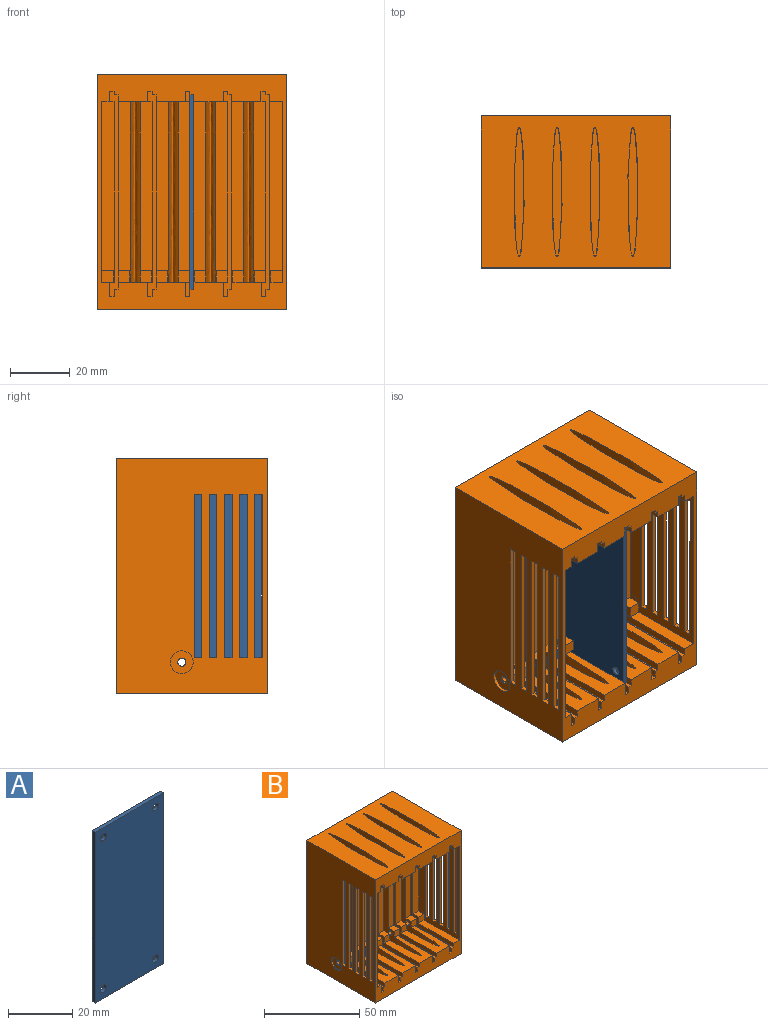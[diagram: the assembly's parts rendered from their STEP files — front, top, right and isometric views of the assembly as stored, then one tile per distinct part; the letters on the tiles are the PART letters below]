
ASSEMBLY  parts=2 mates=1
PART A: 10 faces, bbox 30.1x1.3x65 mm
  f0: plane 64.99x1.33mm, normal (-1,0,0), area 86.7mm2, adj f1,f6,f8,f9
  f1: plane 30.14x1.33mm, normal (0,0,-1), area 40.2mm2, adj f0,f2,f8,f9
  f2: plane 64.99x1.33mm, normal (1,0,0), area 86.7mm2, adj f1,f6,f8,f9
  f3: cylinder r=1.33mm len=2.67mm, axis (0,1,0), area 11.2mm2, adj f8,f9
  f4: cylinder r=1.33mm len=2.67mm, axis (0,1,0), area 11.2mm2, adj f8,f9
  f5: cylinder r=1.33mm len=2.67mm, axis (0,1,0), area 11.2mm2, adj f8,f9
  f6: plane 30.14x1.33mm, normal (0,0,1), area 40.2mm2, adj f0,f2,f8,f9
  f7: cylinder r=1.33mm len=2.67mm, axis (0,1,0), area 11.2mm2, adj f8,f9
  f8: plane 64.99x30.14mm, normal (0,-1,0), area 1936.1mm2, adj f0,f1,f2,f3,f4,f5,f6,f7
  f9: plane 64.99x30.14mm, normal (0,1,0), area 1936.1mm2, adj f0,f1,f2,f3,f4,f5,f6,f7
PART B: 226 faces, bbox 63.5x50.8x79 mm
  f0: plane 30.14x3.22mm, normal (0,0,1), area 76.3mm2, adj f1,f2,f23,f25,f28,f77,f100,f106
  f1: cylinder r=1.38mm len=1mm, axis (1,0,0), area 0.6mm2, adj f0,f23,f106,f223
  f2: cylinder r=1.38mm len=2.71mm, axis (1,0,0), area 2.2mm2, adj f0,f28,f106,f223
  f3: plane 1x0.99mm, normal (-1,0,0), area 0.3mm2, adj f53,f102,f220
  f4: plane 78.99x50.8mm, normal (1,0,0), area 3273.6mm2, adj f98,f99,f100,f101,f176,f177,f178,f179
  f5: plane 2.55x1.31mm, normal (0,0,-1), area 3.4mm2, adj f35,f72,f129,f200
  f6: plane 2.55x1.31mm, normal (0,0,-1), area 3.4mm2, adj f37,f67,f133,f205
  f7: plane 2.55x1.31mm, normal (0,0,-1), area 3.4mm2, adj f39,f62,f137,f210
  f8: plane 2.55x1.31mm, normal (0,0,-1), area 3.4mm2, adj f41,f57,f141,f215
  f9: plane 1x0.99mm, normal (-1,0,0), area 0.3mm2, adj f50,f110,f199
  f10: plane 1x0.99mm, normal (1,0,0), area 0.3mm2, adj f30,f109,f202
  f11: plane 1x0.99mm, normal (-1,0,0), area 0.3mm2, adj f48,f114,f204
  f12: plane 1x0.99mm, normal (1,0,0), area 0.3mm2, adj f31,f113,f207
  f13: plane 1x0.99mm, normal (-1,0,0), area 0.3mm2, adj f46,f118,f209
  f14: plane 1x0.99mm, normal (1,0,0), area 0.3mm2, adj f32,f117,f212
  f15: plane 1x0.99mm, normal (-1,0,0), area 0.3mm2, adj f44,f122,f214
  f16: plane 1x0.99mm, normal (1,0,0), area 0.3mm2, adj f33,f121,f217
  f17: plane 1x0.99mm, normal (1,0,0), area 0.3mm2, adj f53,f102,f219
  f18: plane 1x0.99mm, normal (-1,0,0), area 0.3mm2, adj f53,f102,f219
  f19: extruded ~76.2x43.34mm, area 3513.7mm2, adj f33,f40,f41,f43,f44,f98,f122,f140
  f20: extruded ~76.2x43.34mm, area 3513.7mm2, adj f32,f38,f39,f45,f46,f98,f118,f136
  f21: extruded ~76.2x43.34mm, area 3513.7mm2, adj f31,f36,f37,f47,f48,f98,f114,f132
  f22: extruded ~76.2x43.34mm, area 3513.7mm2, adj f30,f34,f35,f49,f50,f98,f110,f128
  f23: plane 1x0.99mm, normal (1,0,0), area 0.3mm2, adj f0,f1,f106
  f24: plane 3.29x1.44mm, normal (0,0,-1), area 4.6mm2, adj f26,f77,f103,f106,f147,f197
  f25: plane 1x0.99mm, normal (-1,0,0), area 0.3mm2, adj f0,f106,f197
  f26: plane 1x0.99mm, normal (1,0,0), area 0.3mm2, adj f24,f106,f197
  f27: plane 60.39x30.14mm, normal (-1,0,0), area 1120mm2, adj f52,f53,f100,f102,f176,f177,f178,f179
  f28: plane 60.39x30.14mm, normal (1,0,0), area 1120mm2, adj f0,f2,f51,f100,f106,f156,f157,f158
  f29: plane 78.99x50.8mm, normal (-1,0,0), area 3273.6mm2, adj f98,f99,f100,f101,f156,f157,f158,f159
  f30: plane 60.39x4.01mm, normal (0,-1,0), area 229.8mm2, adj f10,f22,f34,f49,f107,f108,f109,f129
  f31: plane 60.39x4.01mm, normal (0,-1,0), area 229.8mm2, adj f12,f21,f36,f47,f111,f112,f113,f133
  f32: plane 60.39x4.01mm, normal (0,-1,0), area 229.8mm2, adj f14,f20,f38,f45,f115,f116,f117,f137
  f33: plane 60.39x4.01mm, normal (0,-1,0), area 229.8mm2, adj f16,f19,f40,f43,f119,f120,f121,f141
  f34: plane 4.23x3.88mm, normal (0,0,1), area 16.3mm2, adj f22,f30,f35,f129
  f35: plane 3.84x3.81mm, normal (0,-1,0), area 14.6mm2, adj f5,f22,f34,f50,f129
  f36: plane 4.23x3.88mm, normal (0,0,1), area 16.3mm2, adj f21,f31,f37,f133
  f37: plane 3.84x3.81mm, normal (0,-1,0), area 14.6mm2, adj f6,f21,f36,f48,f133
  f38: plane 4.23x3.88mm, normal (0,0,1), area 16.3mm2, adj f20,f32,f39,f137
  f39: plane 3.84x3.81mm, normal (0,-1,0), area 14.6mm2, adj f7,f20,f38,f46,f137
  f40: plane 4.23x3.88mm, normal (0,0,1), area 16.3mm2, adj f19,f33,f41,f141
  f41: plane 3.84x3.81mm, normal (0,-1,0), area 14.6mm2, adj f8,f19,f40,f44,f141
  f42: plane 32.44x1.34mm, normal (0,0,1), area 43.4mm2, adj f54,f55,f100,f151
  f43: plane 30.14x9.72mm, normal (0,0,-1), area 218.4mm2, adj f19,f33,f58,f94,f100,f122
  f44: plane 30.14x9.92mm, normal (0,0,1), area 200.1mm2, adj f15,f19,f41,f57,f58,f100,f122,f139
  f45: plane 30.14x9.72mm, normal (0,0,-1), area 218.4mm2, adj f20,f32,f63,f90,f100,f118
  f46: plane 30.14x9.92mm, normal (0,0,1), area 200.1mm2, adj f13,f20,f39,f62,f63,f100,f118,f135
  f47: plane 30.14x9.72mm, normal (0,0,-1), area 218.4mm2, adj f21,f31,f68,f86,f100,f114
  f48: plane 30.14x9.92mm, normal (0,0,1), area 200.1mm2, adj f11,f21,f37,f67,f68,f100,f114,f131
  f49: plane 30.14x9.72mm, normal (0,0,-1), area 218.4mm2, adj f22,f30,f73,f82,f100,f110
  f50: plane 30.14x9.92mm, normal (0,0,1), area 200.1mm2, adj f9,f22,f35,f72,f73,f100,f110,f127
  f51: plane 30.14x2.64mm, normal (0,0,-1), area 79.6mm2, adj f28,f78,f100,f106
  f52: plane 30.14x4.36mm, normal (0,0,-1), area 131.4mm2, adj f27,f54,f100,f102
  f53: plane 30.14x4.67mm, normal (0,0,1), area 115.3mm2, adj f3,f17,f18,f27,f54,f100,f102,f143
  f54: plane 64.99x32.44mm, normal (-1,0,0), area 288.2mm2, adj f42,f52,f53,f97,f100,f102,f151
  f55: plane 32.44x2.41mm, normal (-1,0,0), area 78.2mm2, adj f42,f56,f100,f151
  f56: plane 32.44x1.44mm, normal (0,0,1), area 46.8mm2, adj f55,f57,f100,f151
  f57: plane 32.44x4.71mm, normal (1,0,0), area 152.9mm2, adj f8,f44,f56,f100,f121,f151,f216
  f58: plane 64.99x32.44mm, normal (-1,0,0), area 288.1mm2, adj f43,f44,f59,f93,f100,f122,f150
  f59: plane 32.44x1.34mm, normal (0,0,1), area 43.4mm2, adj f58,f60,f100,f150
  f60: plane 32.44x2.41mm, normal (-1,0,0), area 78.3mm2, adj f59,f61,f100,f150
  f61: plane 32.44x1.44mm, normal (0,0,1), area 46.8mm2, adj f60,f62,f100,f150
  f62: plane 32.44x4.71mm, normal (1,0,0), area 152.9mm2, adj f7,f46,f61,f100,f117,f150,f211
  f63: plane 64.99x32.44mm, normal (-1,0,0), area 288.1mm2, adj f45,f46,f64,f89,f100,f118,f149
  f64: plane 32.44x1.34mm, normal (0,0,1), area 43.4mm2, adj f63,f65,f100,f149
  f65: plane 32.44x2.41mm, normal (-1,0,0), area 78.3mm2, adj f64,f66,f100,f149
  f66: plane 32.44x1.44mm, normal (0,0,1), area 46.8mm2, adj f65,f67,f100,f149
  f67: plane 32.44x4.71mm, normal (1,0,0), area 152.9mm2, adj f6,f48,f66,f100,f113,f149,f206
  f68: plane 64.99x32.44mm, normal (-1,0,0), area 288.1mm2, adj f47,f48,f69,f85,f100,f114,f148
  f69: plane 32.44x1.34mm, normal (0,0,1), area 43.4mm2, adj f68,f70,f100,f148
  f70: plane 32.44x2.41mm, normal (-1,0,0), area 78.3mm2, adj f69,f71,f100,f148
  f71: plane 32.44x1.44mm, normal (0,0,1), area 46.8mm2, adj f70,f72,f100,f148
  f72: plane 32.44x4.71mm, normal (1,0,0), area 152.9mm2, adj f5,f50,f71,f100,f109,f148,f201
  f73: plane 64.99x32.44mm, normal (-1,0,0), area 288.1mm2, adj f49,f50,f74,f81,f100,f110,f147
  f74: plane 32.44x1.34mm, normal (0,0,1), area 43.4mm2, adj f73,f75,f100,f147
  f75: plane 32.44x2.41mm, normal (-1,0,0), area 78.3mm2, adj f74,f76,f100,f147
  f76: plane 32.44x1.44mm, normal (0,0,1), area 46.8mm2, adj f75,f77,f100,f147
  f77: plane 32.44x4.71mm, normal (1,0,0), area 152.9mm2, adj f0,f24,f76,f100,f105,f147
  f78: plane 32.44x3.38mm, normal (1,0,0), area 109.6mm2, adj f51,f79,f100,f104,f147
  f79: plane 32.44x1.65mm, normal (0,0,-1), area 53.4mm2, adj f78,f80,f100,f147
  f80: plane 32.44x1.08mm, normal (-1,0,0), area 34.9mm2, adj f79,f81,f100,f147
  f81: plane 32.44x1.34mm, normal (0,0,-1), area 43.4mm2, adj f73,f80,f100,f147
  f82: plane 32.44x3.38mm, normal (1,0,0), area 109.6mm2, adj f49,f83,f100,f108,f148
  f83: plane 32.44x1.65mm, normal (0,0,-1), area 53.4mm2, adj f82,f84,f100,f148
  f84: plane 32.44x1.08mm, normal (-1,0,0), area 34.9mm2, adj f83,f85,f100,f148
  f85: plane 32.44x1.34mm, normal (0,0,-1), area 43.4mm2, adj f68,f84,f100,f148
  f86: plane 32.44x3.38mm, normal (1,0,0), area 109.6mm2, adj f47,f87,f100,f112,f149
  f87: plane 32.44x1.65mm, normal (0,0,-1), area 53.4mm2, adj f86,f88,f100,f149
  f88: plane 32.44x1.08mm, normal (-1,0,0), area 34.9mm2, adj f87,f89,f100,f149
  f89: plane 32.44x1.34mm, normal (0,0,-1), area 43.4mm2, adj f63,f88,f100,f149
  f90: plane 32.44x3.38mm, normal (1,0,0), area 109.6mm2, adj f45,f91,f100,f116,f150
  f91: plane 32.44x1.65mm, normal (0,0,-1), area 53.4mm2, adj f90,f92,f100,f150
  f92: plane 32.44x1.08mm, normal (-1,0,0), area 34.9mm2, adj f91,f93,f100,f150
  f93: plane 32.44x1.34mm, normal (0,0,-1), area 43.4mm2, adj f58,f92,f100,f150
  f94: plane 32.44x3.38mm, normal (1,0,0), area 109.6mm2, adj f43,f95,f100,f120,f151
  f95: plane 32.44x1.65mm, normal (0,0,-1), area 53.4mm2, adj f94,f96,f100,f151
  f96: plane 32.44x1.08mm, normal (-1,0,0), area 34.9mm2, adj f95,f97,f100,f151
  f97: plane 32.44x1.34mm, normal (0,0,-1), area 43.4mm2, adj f54,f96,f100,f151
  f98: plane 63.5x50.8mm, normal (0,0,1), area 2759.6mm2, adj f4,f19,f20,f21,f22,f29,f100,f101
  f99: plane 63.5x50.8mm, normal (0,0,-1), area 3225.8mm2, adj f4,f29,f100,f101
  f100: plane 78.99x63.5mm, normal (0,-1,0), area 1254.7mm2, adj f0,f4,f27,f28,f29,f42,f43,f44
  f101: plane 78.99x63.5mm, normal (0,1,0), area 5016.1mm2, adj f4,f29,f98,f99
  f102: plane 60.39x4.67mm, normal (0,-1,0), area 248.8mm2, adj f3,f17,f18,f27,f52,f53,f54,f144
  f103: plane 60.39x2.3mm, normal (1,0,0), area 138.8mm2, adj f24,f104,f106,f147
  f104: plane 2.3x1.65mm, normal (0,0,1), area 3.8mm2, adj f78,f103,f106,f147
  f105: plane 2.55x1.33mm, normal (0,0,-1), area 3.4mm2, adj f77,f125,f126,f196
  f106: plane 60.39x4.66mm, normal (0,-1,0), area 246.4mm2, adj f0,f1,f2,f23,f24,f25,f26,f28
  f107: plane 60.39x2.3mm, normal (1,0,0), area 138.8mm2, adj f30,f108,f109,f148
  f108: plane 2.3x1.65mm, normal (0,0,1), area 3.8mm2, adj f30,f82,f107,f148
  f109: plane 3.29x1.44mm, normal (0,0,-1), area 4.6mm2, adj f10,f30,f72,f107,f148,f202
  f110: plane 60.39x4.01mm, normal (0,-1,0), area 230.1mm2, adj f9,f22,f49,f50,f73,f127,f128,f198
  f111: plane 60.39x2.3mm, normal (1,0,0), area 138.8mm2, adj f31,f112,f113,f149
  f112: plane 2.3x1.65mm, normal (0,0,1), area 3.8mm2, adj f31,f86,f111,f149
  f113: plane 3.29x1.44mm, normal (0,0,-1), area 4.6mm2, adj f12,f31,f67,f111,f149,f207
  f114: plane 60.39x4.01mm, normal (0,-1,0), area 230.1mm2, adj f11,f21,f47,f48,f68,f131,f132,f203
  f115: plane 60.39x2.3mm, normal (1,0,0), area 138.8mm2, adj f32,f116,f117,f150
  f116: plane 2.3x1.65mm, normal (0,0,1), area 3.8mm2, adj f32,f90,f115,f150
  f117: plane 3.29x1.44mm, normal (0,0,-1), area 4.6mm2, adj f14,f32,f62,f115,f150,f212
  f118: plane 60.39x4.01mm, normal (0,-1,0), area 230.1mm2, adj f13,f20,f45,f46,f63,f135,f136,f208
  f119: plane 60.39x2.3mm, normal (1,0,0), area 138.8mm2, adj f33,f120,f121,f151
  f120: plane 2.3x1.65mm, normal (0,0,1), area 3.8mm2, adj f33,f94,f119,f151
  f121: plane 3.29x1.44mm, normal (0,0,-1), area 4.6mm2, adj f16,f33,f57,f119,f151,f217
  f122: plane 60.39x4.01mm, normal (0,-1,0), area 230.1mm2, adj f15,f19,f43,f44,f58,f139,f140,f213
  f123: plane 4.23x3.81mm, normal (-1,0,0), area 9.9mm2, adj f0,f106,f124,f126,f196
  f124: plane 4.23x4.06mm, normal (0,0,1), area 17.2mm2, adj f106,f123,f125,f126
  f125: plane 4.23x3.81mm, normal (1,0,0), area 9.9mm2, adj f105,f106,f124,f126,f196
  f126: plane 4.06x3.81mm, normal (0,-1,0), area 15.5mm2, adj f0,f105,f123,f124,f125
  f127: plane 4.23x3.81mm, normal (-1,0,0), area 9.9mm2, adj f50,f110,f128,f130,f198
  f128: plane 4.23x3.9mm, normal (0,0,1), area 16.4mm2, adj f22,f110,f127,f130
  f129: plane 4.23x3.81mm, normal (1,0,0), area 9.9mm2, adj f5,f30,f34,f35,f200
  f130: plane 3.86x3.81mm, normal (0,-1,0), area 14.7mm2, adj f22,f50,f127,f128
  f131: plane 4.23x3.81mm, normal (-1,0,0), area 9.9mm2, adj f48,f114,f132,f134,f203
  f132: plane 4.23x3.9mm, normal (0,0,1), area 16.4mm2, adj f21,f114,f131,f134
  f133: plane 4.23x3.81mm, normal (1,0,0), area 9.9mm2, adj f6,f31,f36,f37,f205
  f134: plane 3.86x3.81mm, normal (0,-1,0), area 14.7mm2, adj f21,f48,f131,f132
  f135: plane 4.23x3.81mm, normal (-1,0,0), area 9.9mm2, adj f46,f118,f136,f138,f208
  f136: plane 4.23x3.9mm, normal (0,0,1), area 16.4mm2, adj f20,f118,f135,f138
  f137: plane 4.23x3.81mm, normal (1,0,0), area 9.9mm2, adj f7,f32,f38,f39,f210
  f138: plane 3.86x3.81mm, normal (0,-1,0), area 14.7mm2, adj f20,f46,f135,f136
  f139: plane 4.23x3.81mm, normal (-1,0,0), area 9.9mm2, adj f44,f122,f140,f142,f213
  f140: plane 4.23x3.9mm, normal (0,0,1), area 16.4mm2, adj f19,f122,f139,f142
  f141: plane 4.23x3.81mm, normal (1,0,0), area 9.9mm2, adj f8,f33,f40,f41,f215
  f142: plane 3.86x3.81mm, normal (0,-1,0), area 14.7mm2, adj f19,f44,f139,f140
  f143: plane 4.06x3.81mm, normal (0,-1,0), area 15.5mm2, adj f53,f144,f145,f146
  f144: plane 4.23x3.81mm, normal (1,0,0), area 9.9mm2, adj f53,f102,f143,f145,f218
  f145: plane 4.23x4.06mm, normal (0,0,1), area 17.2mm2, adj f102,f143,f144,f146
  f146: plane 4.23x3.81mm, normal (-1,0,0), area 9.9mm2, adj f53,f102,f143,f145,f218
  f147: plane 68.48x2.98mm, normal (0,-1,0), area 99.4mm2, adj f24,f73,f74,f75,f76,f77,f78,f79
  f148: plane 68.48x2.98mm, normal (0,-1,0), area 99.4mm2, adj f68,f69,f70,f71,f72,f82,f83,f84
  f149: plane 68.48x2.98mm, normal (0,-1,0), area 99.4mm2, adj f63,f64,f65,f66,f67,f86,f87,f88
  f150: plane 68.48x2.98mm, normal (0,-1,0), area 99.4mm2, adj f58,f59,f60,f61,f62,f90,f91,f92
  f151: plane 68.48x2.98mm, normal (0,-1,0), area 99.4mm2, adj f42,f54,f55,f56,f57,f94,f95,f96
  f152: plane 43.34x3.42mm, normal (0,0,1), area 116.6mm2, adj f19
  f153: plane 43.34x3.42mm, normal (0,0,1), area 116.6mm2, adj f20
  f154: plane 43.34x3.42mm, normal (0,0,1), area 116.6mm2, adj f21
  f155: plane 43.34x3.42mm, normal (0,0,1), area 116.6mm2, adj f22
  f156: plane 54.63x1.39mm, normal (0,1,0), area 76mm2, adj f28,f29,f157,f159
  f157: plane 2.54x1.39mm, normal (0,0,1), area 3.5mm2, adj f28,f29,f156,f158
  f158: plane 54.63x1.39mm, normal (0,-1,0), area 76mm2, adj f28,f29,f157,f159
  f159: plane 2.54x1.39mm, normal (0,0,-1), area 3.5mm2, adj f28,f29,f156,f158
  f160: plane 54.63x1.39mm, normal (0,1,0), area 76mm2, adj f28,f29,f161,f163
  f161: plane 2.54x1.39mm, normal (0,0,1), area 3.5mm2, adj f28,f29,f160,f162
  f162: plane 54.63x1.39mm, normal (0,-1,0), area 76mm2, adj f28,f29,f161,f163
  f163: plane 2.54x1.39mm, normal (0,0,-1), area 3.5mm2, adj f28,f29,f160,f162
  f164: plane 54.63x1.39mm, normal (0,1,0), area 76mm2, adj f28,f29,f165,f167
  f165: plane 2.54x1.39mm, normal (0,0,1), area 3.5mm2, adj f28,f29,f164,f166
  f166: plane 54.63x1.39mm, normal (0,-1,0), area 76mm2, adj f28,f29,f165,f167
  f167: plane 2.54x1.39mm, normal (0,0,-1), area 3.5mm2, adj f28,f29,f164,f166
  f168: plane 54.63x1.39mm, normal (0,1,0), area 76mm2, adj f28,f29,f169,f171
  f169: plane 2.54x1.39mm, normal (0,0,1), area 3.5mm2, adj f28,f29,f168,f170
  f170: plane 54.63x1.39mm, normal (0,-1,0), area 76mm2, adj f28,f29,f169,f171
  f171: plane 2.54x1.39mm, normal (0,0,-1), area 3.5mm2, adj f28,f29,f168,f170
  f172: plane 54.63x1.39mm, normal (0,1,0), area 76mm2, adj f28,f29,f173,f175
  f173: plane 2.54x1.39mm, normal (0,0,1), area 3.5mm2, adj f28,f29,f172,f174
  f174: plane 54.63x1.39mm, normal (0,-1,0), area 76mm2, adj f28,f29,f173,f175
  f175: plane 2.54x1.39mm, normal (0,0,-1), area 3.5mm2, adj f28,f29,f172,f174
  f176: plane 2.54x1.33mm, normal (0,0,-1), area 3.4mm2, adj f4,f27,f177,f179
  f177: plane 54.63x1.39mm, normal (0,-1,0), area 74.1mm2, adj f4,f27,f176,f178
  f178: plane 2.54x1.39mm, normal (0,0,1), area 3.5mm2, adj f4,f27,f177,f179
  f179: plane 54.63x1.39mm, normal (0,1,0), area 74.1mm2, adj f4,f27,f176,f178
  f180: plane 2.54x1.33mm, normal (0,0,-1), area 3.4mm2, adj f4,f27,f181,f183
  f181: plane 54.63x1.39mm, normal (0,-1,0), area 74.1mm2, adj f4,f27,f180,f182
  f182: plane 2.54x1.39mm, normal (0,0,1), area 3.5mm2, adj f4,f27,f181,f183
  f183: plane 54.63x1.39mm, normal (0,1,0), area 74.1mm2, adj f4,f27,f180,f182
  f184: plane 2.54x1.33mm, normal (0,0,-1), area 3.4mm2, adj f4,f27,f185,f187
  f185: plane 54.63x1.39mm, normal (0,-1,0), area 74.1mm2, adj f4,f27,f184,f186
  f186: plane 2.54x1.39mm, normal (0,0,1), area 3.5mm2, adj f4,f27,f185,f187
  f187: plane 54.63x1.39mm, normal (0,1,0), area 74.1mm2, adj f4,f27,f184,f186
  f188: plane 2.54x1.33mm, normal (0,0,-1), area 3.4mm2, adj f4,f27,f189,f191
  f189: plane 54.63x1.39mm, normal (0,-1,0), area 74.1mm2, adj f4,f27,f188,f190
  f190: plane 2.54x1.39mm, normal (0,0,1), area 3.5mm2, adj f4,f27,f189,f191
  f191: plane 54.63x1.39mm, normal (0,1,0), area 74.1mm2, adj f4,f27,f188,f190
  f192: plane 2.54x1.33mm, normal (0,0,-1), area 3.4mm2, adj f4,f27,f193,f195
  f193: plane 54.63x1.39mm, normal (0,-1,0), area 74.1mm2, adj f4,f27,f192,f194
  f194: plane 2.54x1.39mm, normal (0,0,1), area 3.5mm2, adj f4,f27,f193,f195
  f195: plane 54.63x1.39mm, normal (0,1,0), area 74.1mm2, adj f4,f27,f192,f194
  f196: cylinder r=1.38mm len=4.06mm, axis (1,0,0), area 23.5mm2, adj f0,f105,f106,f123,f125
  f197: cylinder r=1.38mm len=4.06mm, axis (1,0,0), area 6mm2, adj f0,f24,f25,f26,f106
  f198: cylinder r=1.38mm len=3.9mm, axis (-1,0,0), area 22.5mm2, adj f22,f50,f110,f127
  f199: cylinder r=1.38mm len=3.9mm, axis (-1,0,0), area 5.7mm2, adj f9,f22,f50,f110
  f200: cylinder r=1.38mm len=3.88mm, axis (-1,0,0), area 22.4mm2, adj f5,f22,f30,f129,f201
  f201: plane 2.55x0.69mm, normal (0,0,1), area 1.8mm2, adj f22,f72,f200,f202
  f202: cylinder r=1.38mm len=3.88mm, axis (-1,0,0), area 5.7mm2, adj f10,f22,f30,f109,f201
  f203: cylinder r=1.38mm len=3.9mm, axis (-1,0,0), area 22.5mm2, adj f21,f48,f114,f131
  f204: cylinder r=1.38mm len=3.9mm, axis (-1,0,0), area 5.7mm2, adj f11,f21,f48,f114
  f205: cylinder r=1.38mm len=3.88mm, axis (-1,0,0), area 22.4mm2, adj f6,f21,f31,f133,f206
  f206: plane 2.55x0.69mm, normal (0,0,1), area 1.8mm2, adj f21,f67,f205,f207
  f207: cylinder r=1.38mm len=3.88mm, axis (-1,0,0), area 5.7mm2, adj f12,f21,f31,f113,f206
  f208: cylinder r=1.38mm len=3.9mm, axis (-1,0,0), area 22.5mm2, adj f20,f46,f118,f135
  f209: cylinder r=1.38mm len=3.9mm, axis (-1,0,0), area 5.7mm2, adj f13,f20,f46,f118
  f210: cylinder r=1.38mm len=3.88mm, axis (-1,0,0), area 22.4mm2, adj f7,f20,f32,f137,f211
  f211: plane 2.55x0.69mm, normal (0,0,1), area 1.8mm2, adj f20,f62,f210,f212
  f212: cylinder r=1.38mm len=3.88mm, axis (-1,0,0), area 5.7mm2, adj f14,f20,f32,f117,f211
  f213: cylinder r=1.38mm len=3.9mm, axis (-1,0,0), area 22.5mm2, adj f19,f44,f122,f139
  f214: cylinder r=1.38mm len=3.9mm, axis (-1,0,0), area 5.7mm2, adj f15,f19,f44,f122
  f215: cylinder r=1.38mm len=3.88mm, axis (-1,0,0), area 22.4mm2, adj f8,f19,f33,f141,f216
  f216: plane 2.55x0.69mm, normal (0,0,1), area 1.8mm2, adj f19,f57,f215,f217
  f217: cylinder r=1.38mm len=3.88mm, axis (-1,0,0), area 5.7mm2, adj f16,f19,f33,f121,f216
  f218: cylinder r=1.38mm len=4.06mm, axis (-1,0,0), area 23.5mm2, adj f53,f102,f144,f146
  f219: cylinder r=1.38mm len=4.06mm, axis (-1,0,0), area 6mm2, adj f17,f18,f53,f102
  f220: cylinder r=1.38mm len=1mm, axis (-1,0,0), area 0.6mm2, adj f3,f53,f102,f225
  f221: cylinder r=1.38mm len=2.71mm, axis (-1,0,0), area 2.2mm2, adj f27,f53,f102,f225
  f222: cylinder r=3.81mm len=7.62mm, axis (-1,0,0), area 24.3mm2, adj f29,f223
  f223: plane 7.62x7.62mm, normal (-1,0,0), area 39.7mm2, adj f0,f1,f2,f106,f222
  f224: cylinder r=3.81mm len=7.62mm, axis (1,0,0), area 24.3mm2, adj f4,f225
  f225: plane 7.62x7.62mm, normal (1,0,0), area 39.7mm2, adj f53,f102,f220,f221,f224
PLACE A rot(axis=(0,0,-1),90deg) t=(13.37,58.81,32.34)mm
PLACE B t=(13.94,21.2,32.33)mm fixed
MATE slider A.f0 <-> B.f149  axis (0,1,0) through (12.71,2.82,32.34)mm
